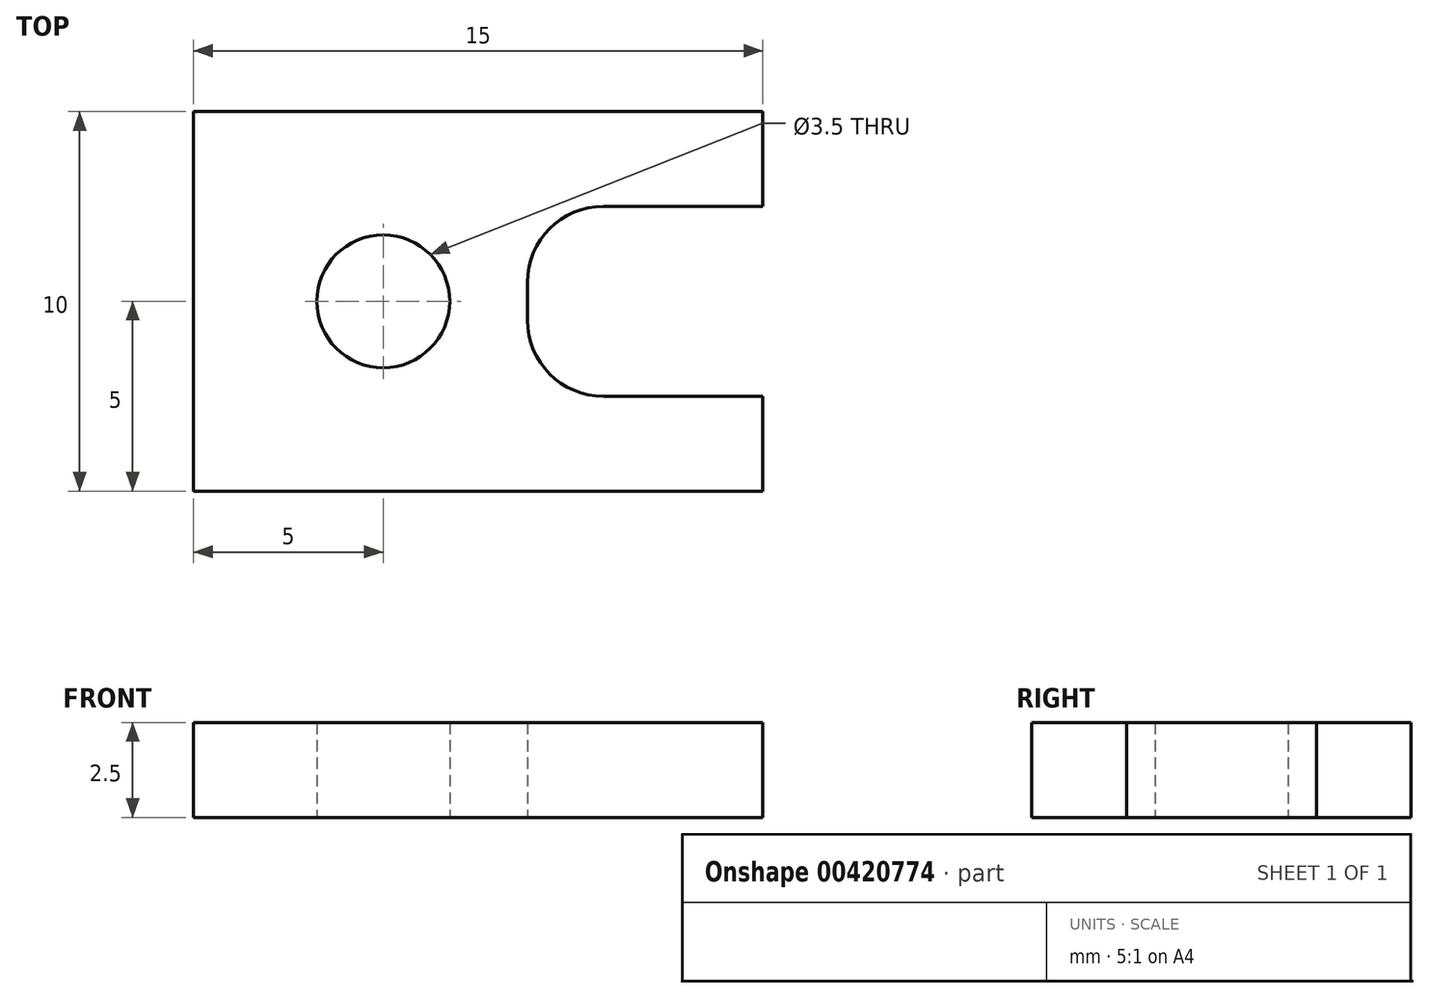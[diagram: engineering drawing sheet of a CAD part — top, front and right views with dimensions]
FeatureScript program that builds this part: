
annotation { "Feature Type Name" : "Feature", "Feature Type Description" : "" }
export const myFeature = defineFeature(function(context is Context, id is Id, definition is map)
    precondition{}
    {
        {
            var Q0;
            Q0=qCreatedBy(makeId("Top.planeOp"),FACE);
            var sketch = newSketch(context, id + "F0", { "sketchPlane" : qUnion([Q0])});
            skLineSegment(sketch, "E0.bottom", {"start": v(-5, 5) * mm, "end": v(10, 5) * mm});
            skLineSegment(sketch, "E0.top", {"start": v(-5, -5) * mm, "end": v(10, -5) * mm});
            skLineSegment(sketch, "E0.left", {"start": v(-5, 5) * mm, "end": v(-5, -5) * mm});
            skLineSegment(sketch, "E0.right", {"start": v(10, 5) * mm, "end": v(10, -5) * mm});
            skCircle(sketch, "E1", {"center": v(0, 0) * mm, "radius": 1.75 * mm});
            skLineSegment(sketch, "E2.bottom", {"start": v(10, 2.5) * mm, "end": v(3.8, 2.5) * mm});
            skLineSegment(sketch, "E2.top", {"start": v(10, -2.5) * mm, "end": v(3.8, -2.5) * mm});
            skLineSegment(sketch, "E2.left", {"start": v(10, 2.5) * mm, "end": v(10, -2.5) * mm});
            skLineSegment(sketch, "E2.right", {"start": v(3.8, 2.5) * mm, "end": v(3.8, -2.5) * mm});
            skSolve(sketch);
        }
        {
            var Q0;
            {var subQ1=sQuery(id+"F0.wireOp",EDGE,"E0.bottom");Q0=makeQuery(id+"F0.imprint","IMPRINT",FACE,{"disambiguationData":[TD([[makeQuery(id+"F0.imprint","IMPRINT",EDGE,{"derivedFrom":subQ1}),-1.0]])]});}
            extrude(context, id + "F1", {"entities" : qUnion([Q0]), "depth" : 2.5 * mm});
        }
        {
            var Q0;
            Q0=makeQuery(id+"F1.opExtrude","SWEPT_EDGE",EDGE,{"disambiguationData":[OSD([sQuery(id+"F0.wireOp",EDGE,"E2.bottom"),sQuery(id+"F0.wireOp",EDGE,"E2.right")])]});
            fillet(context, id + "F2", {"entities" : qUnion([Q0]), "radius" : 2 * mm, "tangentPropagation" : true, "allowEdgeOverflow" : false});
        }
        {
            var Q0;
            Q0=makeQuery(id+"F1.opExtrude","SWEPT_EDGE",EDGE,{"disambiguationData":[OSD([sQuery(id+"F0.wireOp",EDGE,"E2.top"),sQuery(id+"F0.wireOp",EDGE,"E2.right")])]});
            fillet(context, id + "F3", {"entities" : qUnion([Q0]), "radius" : 2 * mm, "tangentPropagation" : true, "allowEdgeOverflow" : false});
        }
    });
